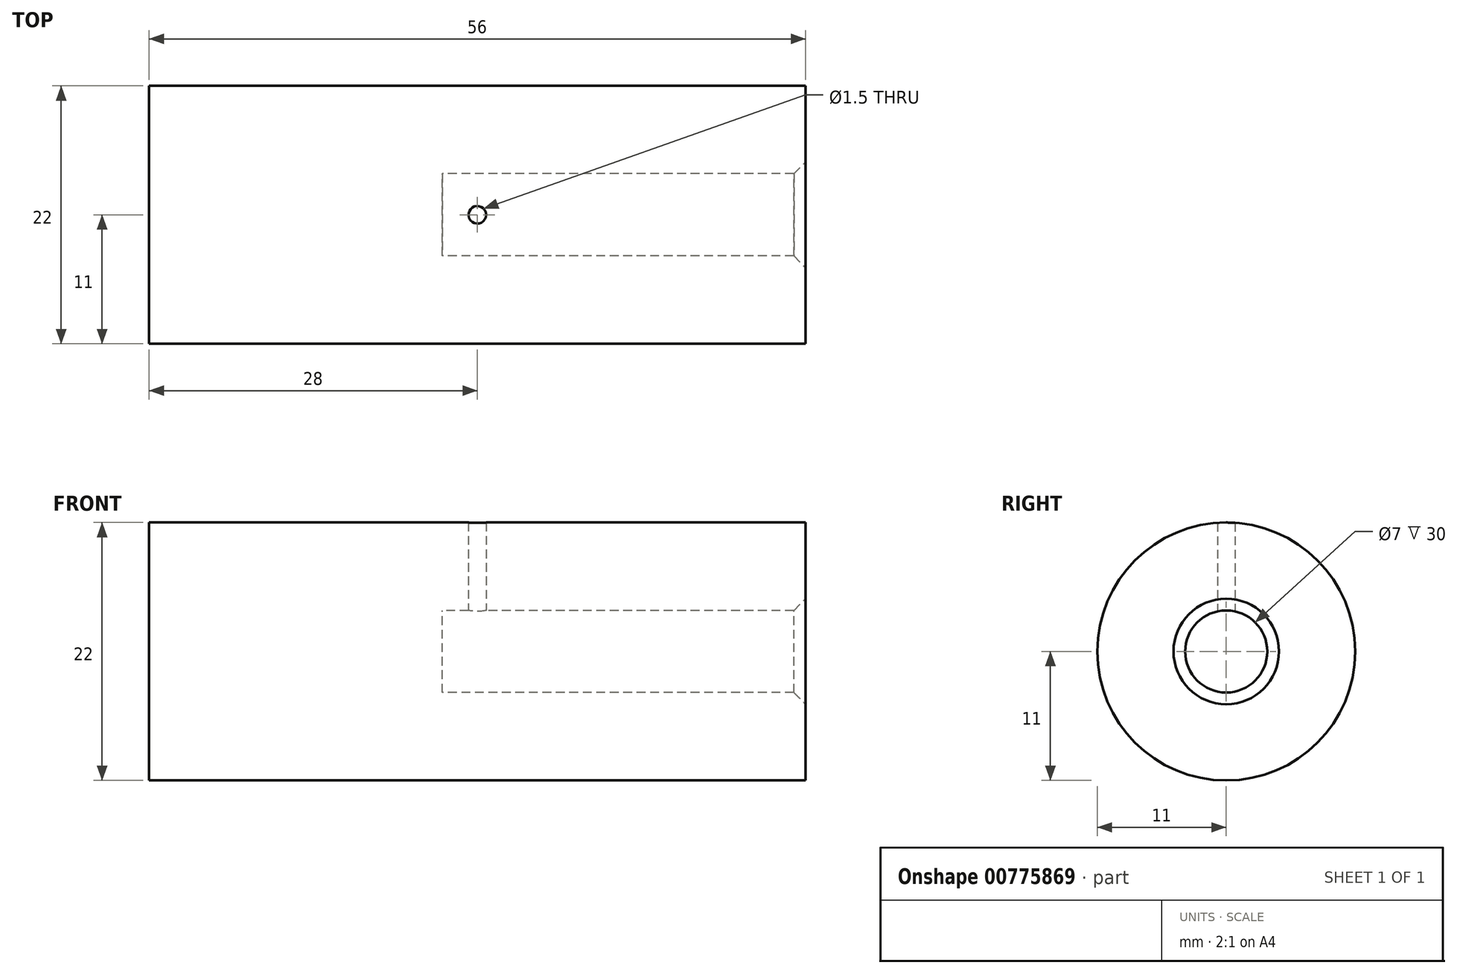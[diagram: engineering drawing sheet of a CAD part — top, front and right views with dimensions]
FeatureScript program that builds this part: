
annotation { "Feature Type Name" : "Feature", "Feature Type Description" : "" }
export const myFeature = defineFeature(function(context is Context, id is Id, definition is map)
    precondition{}
    {
        {
            var Q0;
            Q0=qCreatedBy(makeId("Right.planeOp"),FACE);
            var sketch = newSketch(context, id + "F0", { "sketchPlane" : qUnion([Q0])});
            skCircle(sketch, "E0", {"center": v(0, 0) * mm, "radius": 11 * mm});
            skCircle(sketch, "E1", {"center": v(0, 0) * mm, "radius": 3.5 * mm});
            skSolve(sketch);
        }
        {
            var Q0;
            Q0=makeQuery(id+"F0.imprint","IMPRINT",FACE,{"disambiguationData":[TD([[makeQuery(id+"F0.imprint","IMPRINT",EDGE,{"derivedFrom":sQuery(id+"F0.wireOp",EDGE,"E1")}),1.0]])]});
            extrude(context, id + "F1", {"entities" : qUnion([Q0]), "oppositeDirection" : true, "depth" : 28 * mm, "offsetDistance" : 25.4 * mm, "hasSecondDirection" : true, "secondDirectionOppositeDirection" : true, "secondDirectionDepth" : 3 * mm});
        }
        {
            var Q0;
            Q0=makeQuery(id+"F0.imprint","IMPRINT",FACE,{"disambiguationData":[TD([[makeQuery(id+"F0.imprint","IMPRINT",EDGE,{"derivedFrom":sQuery(id+"F0.wireOp",EDGE,"E0")}),1.0]])]});
            extrude(context, id + "F2", {"entities" : qUnion([Q0]), "operationType" : NewBodyOperationType.ADD, "endBound" : BoundingType.SYMMETRIC, "depth" : 56 * mm, "offsetDistance" : 25.4 * mm});
        }
        {
            var Q0;
            Q0=qCreatedBy(makeId("Top.planeOp"),FACE);
            var sketch = newSketch(context, id + "F3", { "sketchPlane" : qUnion([Q0])});
            skCircle(sketch, "E2", {"center": v(0, 0) * mm, "radius": 0.75 * mm});
            skSolve(sketch);
        }
        {
            var Q0;
            Q0=makeQuery(id+"F3.imprint","IMPRINT",FACE,{"disambiguationData":[TD([[makeQuery(id+"F3.imprint","IMPRINT",EDGE,{"derivedFrom":sQuery(id+"F3.wireOp",EDGE,"E2")}),1.0]])]});
            var Q1;
            Q1=sQuery(id+"F3.wireOp",EDGE,"E2");
            extrude(context, id + "F4", {"entities" : qUnion([Q0]), "operationType" : NewBodyOperationType.REMOVE, "surfaceEntities" : qUnion([Q1]), "depth" : 12.7 * mm, "offsetDistance" : 25.4 * mm});
        }
        {
            var Q0;
            Q0=makeQuery(id+"F2.opExtrude","CAP_EDGE",EDGE,{"disambiguationData":[OSD([sQuery(id+"F0.wireOp",EDGE,"E1")])],"isStart":false});
            chamfer(context, id + "F5", {"entities" : qUnion([Q0]), "width" : 1 * mm});
        }
    });
